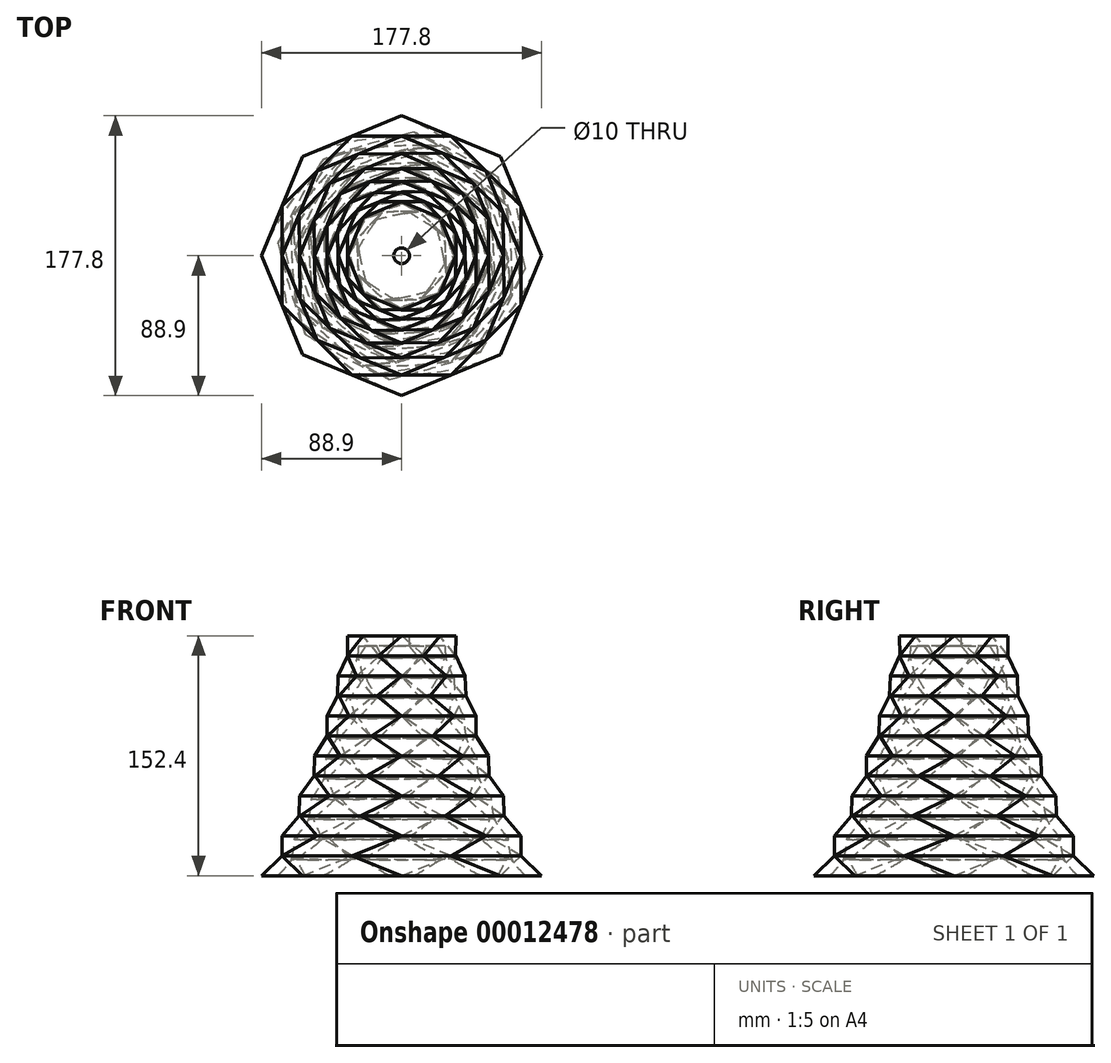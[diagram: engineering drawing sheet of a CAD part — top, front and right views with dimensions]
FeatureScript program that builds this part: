
annotation { "Feature Type Name" : "Feature", "Feature Type Description" : "" }
export const myFeature = defineFeature(function(context is Context, id is Id, definition is map)
    precondition{}
    {
        {
            var Q0;
            Q0=qCreatedBy(makeId("Top.planeOp"),FACE);
            var sketch = newSketch(context, id + "F0", { "sketchPlane" : qUnion([Q0])});
            skLineSegment(sketch, "E0.rect.bottom", {"start": v(88.9, -88.9) * mm, "end": v(-88.9, -88.9) * mm, "construction": true});
            skLineSegment(sketch, "E0.rect.top", {"start": v(88.9, 88.9) * mm, "end": v(-88.9, 88.9) * mm, "construction": true});
            skLineSegment(sketch, "E0.rect.left", {"start": v(88.9, -88.9) * mm, "end": v(88.9, 88.9) * mm, "construction": true});
            skLineSegment(sketch, "E0.rect.right", {"start": v(-88.9, -88.9) * mm, "end": v(-88.9, 88.9) * mm, "construction": true});
            skPoint(sketch, "E0.rect.middle", {"position": v(0, 0) * mm});
            skCircle(sketch, "E1.cCircle", {"center": v(0, 0) * mm, "radius": 88.9 * mm, "construction": true});
            skLineSegment(sketch, "E1.0", {"start": v(88.9, 0) * mm, "end": v(62.86, -62.86) * mm});
            skLineSegment(sketch, "E1.1", {"start": v(62.86, -62.86) * mm, "end": v(0, -88.9) * mm});
            skLineSegment(sketch, "E1.2", {"start": v(0, -88.9) * mm, "end": v(-62.86, -62.86) * mm});
            skLineSegment(sketch, "E1.3", {"start": v(-62.86, -62.86) * mm, "end": v(-88.9, 0) * mm});
            skLineSegment(sketch, "E1.4", {"start": v(-88.9, 0) * mm, "end": v(-62.86, 62.86) * mm});
            skLineSegment(sketch, "E1.5", {"start": v(-62.86, 62.86) * mm, "end": v(0, 88.9) * mm});
            skLineSegment(sketch, "E1.6", {"start": v(0, 88.9) * mm, "end": v(62.86, 62.86) * mm});
            skLineSegment(sketch, "E1.7", {"start": v(62.86, 62.86) * mm, "end": v(88.9, 0) * mm});
            skSolve(sketch);
        }
        {
            var Q0;
            Q0=qCreatedBy(makeId("Top.planeOp"),FACE);
            cPlane(context, id + "F1", {"entities" : qUnion([Q0]), "cplaneType" : CPlaneType.OFFSET, "offset" : 12.7 * mm, "width" : 152.4 * mm, "height" : 152.4 * mm});
        }
        {
            var Q0;
            Q0=qCreatedBy(id+"F1.planeOp",FACE);
            var sketch = newSketch(context, id + "F2", { "sketchPlane" : qUnion([Q0])});
            skPoint(sketch, "E2.0", {"position": v(0, 0) * mm});
            skCircle(sketch, "E3.cCircle", {"center": v(0, 0) * mm, "radius": 82.13 * mm, "construction": true});
            skLineSegment(sketch, "E3.0", {"start": v(75.88, -31.43) * mm, "end": v(31.43, -75.88) * mm});
            skLineSegment(sketch, "E3.1", {"start": v(31.43, -75.88) * mm, "end": v(-31.43, -75.88) * mm});
            skLineSegment(sketch, "E3.2", {"start": v(-31.43, -75.88) * mm, "end": v(-75.88, -31.43) * mm});
            skLineSegment(sketch, "E3.3", {"start": v(-75.88, -31.43) * mm, "end": v(-75.88, 31.43) * mm});
            skLineSegment(sketch, "E3.4", {"start": v(-75.88, 31.43) * mm, "end": v(-31.43, 75.88) * mm});
            skLineSegment(sketch, "E3.5", {"start": v(-31.43, 75.88) * mm, "end": v(31.43, 75.88) * mm});
            skLineSegment(sketch, "E3.6", {"start": v(31.43, 75.88) * mm, "end": v(75.88, 31.43) * mm});
            skLineSegment(sketch, "E3.7", {"start": v(75.88, 31.43) * mm, "end": v(75.88, -31.43) * mm});
            skSolve(sketch);
        }
        {
            var Q0;
            Q0=makeQuery(id+"F0.imprint","IMPRINT",FACE,{"disambiguationData":[TD([[makeQuery(id+"F0.imprint","IMPRINT",EDGE,{"derivedFrom":sQuery(id+"F0.wireOp",EDGE,"E1.0")}),-1.0]])]});
            var Q1;
            Q1=makeQuery(id+"F2.imprint","IMPRINT",FACE,{"disambiguationData":[TD([[makeQuery(id+"F2.imprint","IMPRINT",EDGE,{"derivedFrom":sQuery(id+"F2.wireOp",EDGE,"E3.0")}),-1.0]])]});
            loft(context, id + "F3", {"sheetProfilesArray" : [{ "sheetProfileEntities" : qUnion([Q0]) }, { "sheetProfileEntities" : qUnion([Q1]) }]});
        }
        {
            var Q0;
            Q0=qCreatedBy(id+"F1.planeOp",FACE);
            cPlane(context, id + "F4", {"entities" : qUnion([Q0]), "cplaneType" : CPlaneType.OFFSET, "offset" : 12.7 * mm, "width" : 152.4 * mm, "height" : 152.4 * mm});
        }
        {
            var Q0;
            Q0=qCreatedBy(id+"F4.planeOp",FACE);
            var sketch = newSketch(context, id + "F5", { "sketchPlane" : qUnion([Q0])});
            skFitSpline(sketch, "E4.0", {"points": [v(75.88, -31.43) * mm, v(75.88, -10.48) * mm, v(75.88, 10.48) * mm, v(75.88, 31.43) * mm]});
            skCircle(sketch, "E5.cCircle", {"center": v(0, 0) * mm, "radius": 75.88 * mm, "construction": true});
            skLineSegment(sketch, "E5.0", {"start": v(75.88, 0) * mm, "end": v(53.66, -53.66) * mm});
            skLineSegment(sketch, "E5.1", {"start": v(53.66, -53.66) * mm, "end": v(0, -75.88) * mm});
            skLineSegment(sketch, "E5.2", {"start": v(0, -75.88) * mm, "end": v(-53.66, -53.66) * mm});
            skLineSegment(sketch, "E5.3", {"start": v(-53.66, -53.66) * mm, "end": v(-75.88, 0) * mm});
            skLineSegment(sketch, "E5.4", {"start": v(-75.88, 0) * mm, "end": v(-53.66, 53.66) * mm});
            skLineSegment(sketch, "E5.5", {"start": v(-53.66, 53.66) * mm, "end": v(0, 75.88) * mm});
            skLineSegment(sketch, "E5.6", {"start": v(0, 75.88) * mm, "end": v(53.66, 53.66) * mm});
            skLineSegment(sketch, "E5.7", {"start": v(53.66, 53.66) * mm, "end": v(75.88, 0) * mm});
            skSolve(sketch);
        }
        {
            var Q1;
            Q1=makeQuery(id+"F3.opLoft","CAP_FACE",FACE,{"disambiguationData":[OSD([makeQuery(id+"F2.imprint","IMPRINT",FACE,{"disambiguationData":[TD([[makeQuery(id+"F2.imprint","IMPRINT",EDGE,{"derivedFrom":sQuery(id+"F2.wireOp",EDGE,"E3.0")}),-1.0]])]})])],"isStart":true});
            var Q2;
            Q2=makeQuery(id+"F5.imprint","IMPRINT",FACE,{"disambiguationData":[TD([[makeQuery(id+"F5.imprint","IMPRINT",EDGE,{"derivedFrom":sQuery(id+"F5.wireOp",EDGE,"E5.0")}),-1.0]])]});
            loft(context, id + "F6", {"operationType" : NewBodyOperationType.ADD, "sheetProfilesArray" : [{ "sheetProfileEntities" : qUnion([Q1]) }, { "sheetProfileEntities" : qUnion([Q2]) }]});
        }
        {
            var Q0;
            Q0=qCreatedBy(id+"F4.planeOp",FACE);
            cPlane(context, id + "F7", {"entities" : qUnion([Q0]), "cplaneType" : CPlaneType.OFFSET, "offset" : 12.7 * mm, "width" : 152.4 * mm, "height" : 152.4 * mm});
        }
        {
            var Q0;
            Q0=qCreatedBy(id+"F7.planeOp",FACE);
            var sketch = newSketch(context, id + "F8", { "sketchPlane" : qUnion([Q0])});
            skCircle(sketch, "E6.cCircle", {"center": v(0, 0) * mm, "radius": 70.1 * mm, "construction": true});
            skLineSegment(sketch, "E6.0", {"start": v(64.47, 27.56) * mm, "end": v(65.07, -26.1) * mm});
            skLineSegment(sketch, "E6.1", {"start": v(65.07, -26.1) * mm, "end": v(27.56, -64.47) * mm});
            skLineSegment(sketch, "E6.2", {"start": v(27.56, -64.47) * mm, "end": v(-26.1, -65.07) * mm});
            skLineSegment(sketch, "E6.3", {"start": v(-26.1, -65.07) * mm, "end": v(-64.47, -27.56) * mm});
            skLineSegment(sketch, "E6.4", {"start": v(-64.47, -27.56) * mm, "end": v(-65.07, 26.1) * mm});
            skLineSegment(sketch, "E6.5", {"start": v(-65.07, 26.1) * mm, "end": v(-27.56, 64.47) * mm});
            skLineSegment(sketch, "E6.6", {"start": v(-27.56, 64.47) * mm, "end": v(26.1, 65.07) * mm});
            skLineSegment(sketch, "E6.7", {"start": v(26.1, 65.07) * mm, "end": v(64.47, 27.56) * mm});
            skSolve(sketch);
        }
        {
            var Q1;
            Q1=makeQuery(id+"F6.opLoft","CAP_FACE",FACE,{"disambiguationData":[OSD([makeQuery(id+"F5.imprint","IMPRINT",FACE,{"disambiguationData":[TD([[makeQuery(id+"F5.imprint","IMPRINT",EDGE,{"derivedFrom":sQuery(id+"F5.wireOp",EDGE,"E5.0")}),-1.0]])]})])],"isStart":true});
            var Q2;
            Q2=makeQuery(id+"F8.imprint","IMPRINT",FACE,{"disambiguationData":[TD([[makeQuery(id+"F8.imprint","IMPRINT",EDGE,{"derivedFrom":sQuery(id+"F8.wireOp",EDGE,"E6.0")}),-1.0]])]});
            loft(context, id + "F9", {"operationType" : NewBodyOperationType.ADD, "sheetProfilesArray" : [{ "sheetProfileEntities" : qUnion([Q1]) }, { "sheetProfileEntities" : qUnion([Q2]) }]});
        }
        {
            var Q0;
            Q0=qCreatedBy(id+"F7.planeOp",FACE);
            cPlane(context, id + "F10", {"entities" : qUnion([Q0]), "cplaneType" : CPlaneType.OFFSET, "offset" : 12.7 * mm, "width" : 152.4 * mm, "height" : 152.4 * mm});
        }
        {
            var Q0;
            Q0=qCreatedBy(id+"F10.planeOp",FACE);
            var sketch = newSketch(context, id + "F11", { "sketchPlane" : qUnion([Q0])});
            skCircle(sketch, "E7.cCircle", {"center": v(0, 0) * mm, "radius": 64.78 * mm, "construction": true});
            skLineSegment(sketch, "E7.0", {"start": v(-64.78, 0) * mm, "end": v(-45.8, 45.8) * mm});
            skLineSegment(sketch, "E7.1", {"start": v(-45.8, 45.8) * mm, "end": v(0, 64.78) * mm});
            skLineSegment(sketch, "E7.2", {"start": v(0, 64.78) * mm, "end": v(45.8, 45.8) * mm});
            skLineSegment(sketch, "E7.3", {"start": v(45.8, 45.8) * mm, "end": v(64.78, 0) * mm});
            skLineSegment(sketch, "E7.4", {"start": v(64.78, 0) * mm, "end": v(45.8, -45.8) * mm});
            skLineSegment(sketch, "E7.5", {"start": v(45.8, -45.8) * mm, "end": v(0, -64.78) * mm});
            skLineSegment(sketch, "E7.6", {"start": v(0, -64.78) * mm, "end": v(-45.8, -45.8) * mm});
            skLineSegment(sketch, "E7.7", {"start": v(-45.8, -45.8) * mm, "end": v(-64.78, 0) * mm});
            skSolve(sketch);
        }
        {
            var Q1;
            Q1=makeQuery(id+"F9.opLoft","CAP_FACE",FACE,{"disambiguationData":[OSD([makeQuery(id+"F8.imprint","IMPRINT",FACE,{"disambiguationData":[TD([[makeQuery(id+"F8.imprint","IMPRINT",EDGE,{"derivedFrom":sQuery(id+"F8.wireOp",EDGE,"E6.0")}),-1.0]])]})])],"isStart":true});
            var Q2;
            Q2=makeQuery(id+"F11.imprint","IMPRINT",FACE,{"disambiguationData":[TD([[makeQuery(id+"F11.imprint","IMPRINT",EDGE,{"derivedFrom":sQuery(id+"F11.wireOp",EDGE,"E7.0")}),-1.0]])]});
            loft(context, id + "F12", {"operationType" : NewBodyOperationType.ADD, "sheetProfilesArray" : [{ "sheetProfileEntities" : qUnion([Q1]) }, { "sheetProfileEntities" : qUnion([Q2]) }]});
        }
        {
            var Q0;
            Q0=qCreatedBy(id+"F10.planeOp",FACE);
            cPlane(context, id + "F13", {"entities" : qUnion([Q0]), "cplaneType" : CPlaneType.OFFSET, "offset" : 12.7 * mm, "width" : 152.4 * mm, "height" : 152.4 * mm});
        }
        {
            var Q0;
            Q0=qCreatedBy(id+"F13.planeOp",FACE);
            var sketch = newSketch(context, id + "F14", { "sketchPlane" : qUnion([Q0])});
            skFitSpline(sketch, "E8.0", {"points": [v(64.78, 0) * mm, v(58.45, 15.27) * mm, v(52.13, 30.54) * mm, v(45.8, 45.8) * mm]});
            skCircle(sketch, "E9.cCircle", {"center": v(0, 0) * mm, "radius": 59.85 * mm, "construction": true});
            skLineSegment(sketch, "E9.0", {"start": v(55.07, 23.43) * mm, "end": v(55.51, -22.37) * mm});
            skLineSegment(sketch, "E9.1", {"start": v(55.51, -22.37) * mm, "end": v(23.43, -55.07) * mm});
            skLineSegment(sketch, "E9.2", {"start": v(23.43, -55.07) * mm, "end": v(-22.37, -55.51) * mm});
            skLineSegment(sketch, "E9.3", {"start": v(-22.37, -55.51) * mm, "end": v(-55.07, -23.43) * mm});
            skLineSegment(sketch, "E9.4", {"start": v(-55.07, -23.43) * mm, "end": v(-55.51, 22.37) * mm});
            skLineSegment(sketch, "E9.5", {"start": v(-55.51, 22.37) * mm, "end": v(-23.43, 55.07) * mm});
            skLineSegment(sketch, "E9.6", {"start": v(-23.43, 55.07) * mm, "end": v(22.37, 55.51) * mm});
            skLineSegment(sketch, "E9.7", {"start": v(22.37, 55.51) * mm, "end": v(55.07, 23.43) * mm});
            skSolve(sketch);
        }
        {
            var Q1;
            Q1=makeQuery(id+"F12.opLoft","CAP_FACE",FACE,{"disambiguationData":[OSD([makeQuery(id+"F11.imprint","IMPRINT",FACE,{"disambiguationData":[TD([[makeQuery(id+"F11.imprint","IMPRINT",EDGE,{"derivedFrom":sQuery(id+"F11.wireOp",EDGE,"E7.0")}),-1.0]])]})])],"isStart":true});
            var Q2;
            Q2=makeQuery(id+"F14.imprint","IMPRINT",FACE,{"disambiguationData":[TD([[makeQuery(id+"F14.imprint","IMPRINT",EDGE,{"derivedFrom":sQuery(id+"F14.wireOp",EDGE,"E9.0")}),-1.0]])]});
            loft(context, id + "F15", {"operationType" : NewBodyOperationType.ADD, "sheetProfilesArray" : [{ "sheetProfileEntities" : qUnion([Q1]) }, { "sheetProfileEntities" : qUnion([Q2]) }]});
        }
        {
            var Q0;
            Q0=qCreatedBy(id+"F13.planeOp",FACE);
            cPlane(context, id + "F16", {"entities" : qUnion([Q0]), "cplaneType" : CPlaneType.OFFSET, "offset" : 12.7 * mm, "width" : 152.4 * mm, "height" : 152.4 * mm});
        }
        {
            var Q0;
            Q0=qCreatedBy(id+"F16.planeOp",FACE);
            var sketch = newSketch(context, id + "F17", { "sketchPlane" : qUnion([Q0])});
            skFitSpline(sketch, "E10.0", {"points": [v(55.51, -22.37) * mm, v(55.36, -7.1) * mm, v(55.22, 8.17) * mm, v(55.07, 23.43) * mm]});
            skCircle(sketch, "E11.cCircle", {"center": v(0, 0) * mm, "radius": 55.3 * mm, "construction": true});
            skLineSegment(sketch, "E11.0", {"start": v(55.3, 0) * mm, "end": v(39.1, -39.1) * mm});
            skLineSegment(sketch, "E11.1", {"start": v(39.1, -39.1) * mm, "end": v(0, -55.3) * mm});
            skLineSegment(sketch, "E11.2", {"start": v(0, -55.3) * mm, "end": v(-39.1, -39.1) * mm});
            skLineSegment(sketch, "E11.3", {"start": v(-39.1, -39.1) * mm, "end": v(-55.3, 0) * mm});
            skLineSegment(sketch, "E11.4", {"start": v(-55.3, 0) * mm, "end": v(-39.1, 39.1) * mm});
            skLineSegment(sketch, "E11.5", {"start": v(-39.1, 39.1) * mm, "end": v(0, 55.3) * mm});
            skLineSegment(sketch, "E11.6", {"start": v(0, 55.3) * mm, "end": v(39.1, 39.1) * mm});
            skLineSegment(sketch, "E11.7", {"start": v(39.1, 39.1) * mm, "end": v(55.3, 0) * mm});
            skSolve(sketch);
        }
        {
            var Q1;
            Q1=makeQuery(id+"F15.opLoft","CAP_FACE",FACE,{"disambiguationData":[OSD([makeQuery(id+"F14.imprint","IMPRINT",FACE,{"disambiguationData":[TD([[makeQuery(id+"F14.imprint","IMPRINT",EDGE,{"derivedFrom":sQuery(id+"F14.wireOp",EDGE,"E9.0")}),-1.0]])]})])],"isStart":true});
            var Q2;
            Q2=makeQuery(id+"F17.imprint","IMPRINT",FACE,{"disambiguationData":[TD([[makeQuery(id+"F17.imprint","IMPRINT",EDGE,{"derivedFrom":sQuery(id+"F17.wireOp",EDGE,"E11.0")}),-1.0]])]});
            loft(context, id + "F18", {"operationType" : NewBodyOperationType.ADD, "sheetProfilesArray" : [{ "sheetProfileEntities" : qUnion([Q1]) }, { "sheetProfileEntities" : qUnion([Q2]) }]});
        }
        {
            var Q0;
            Q0=qCreatedBy(id+"F16.planeOp",FACE);
            cPlane(context, id + "F19", {"entities" : qUnion([Q0]), "cplaneType" : CPlaneType.OFFSET, "offset" : 12.7 * mm, "width" : 152.4 * mm, "height" : 152.4 * mm});
        }
        {
            var Q0;
            Q0=qCreatedBy(id+"F19.planeOp",FACE);
            var sketch = newSketch(context, id + "F20", { "sketchPlane" : qUnion([Q0])});
            skCircle(sketch, "E12.cCircle", {"center": v(0, 0) * mm, "radius": 51.09 * mm, "construction": true});
            skLineSegment(sketch, "E12.0", {"start": v(46.97, 20.1) * mm, "end": v(47.43, -19) * mm});
            skLineSegment(sketch, "E12.1", {"start": v(47.43, -19) * mm, "end": v(20.1, -46.97) * mm});
            skLineSegment(sketch, "E12.2", {"start": v(20.1, -46.97) * mm, "end": v(-19, -47.43) * mm});
            skLineSegment(sketch, "E12.3", {"start": v(-19, -47.43) * mm, "end": v(-46.97, -20.1) * mm});
            skLineSegment(sketch, "E12.4", {"start": v(-46.97, -20.1) * mm, "end": v(-47.43, 19) * mm});
            skLineSegment(sketch, "E12.5", {"start": v(-47.43, 19) * mm, "end": v(-20.1, 46.97) * mm});
            skLineSegment(sketch, "E12.6", {"start": v(-20.1, 46.97) * mm, "end": v(19, 47.43) * mm});
            skLineSegment(sketch, "E12.7", {"start": v(19, 47.43) * mm, "end": v(46.97, 20.1) * mm});
            skSolve(sketch);
        }
        {
            var Q1;
            Q1=makeQuery(id+"F18.opLoft","CAP_FACE",FACE,{"disambiguationData":[OSD([makeQuery(id+"F17.imprint","IMPRINT",FACE,{"disambiguationData":[TD([[makeQuery(id+"F17.imprint","IMPRINT",EDGE,{"derivedFrom":sQuery(id+"F17.wireOp",EDGE,"E11.0")}),-1.0]])]})])],"isStart":true});
            var Q2;
            Q2=makeQuery(id+"F20.imprint","IMPRINT",FACE,{"disambiguationData":[TD([[makeQuery(id+"F20.imprint","IMPRINT",EDGE,{"derivedFrom":sQuery(id+"F20.wireOp",EDGE,"E12.0")}),-1.0]])]});
            loft(context, id + "F21", {"operationType" : NewBodyOperationType.ADD, "sheetProfilesArray" : [{ "sheetProfileEntities" : qUnion([Q1]) }, { "sheetProfileEntities" : qUnion([Q2]) }]});
        }
        {
            var Q0;
            Q0=qCreatedBy(id+"F19.planeOp",FACE);
            cPlane(context, id + "F22", {"entities" : qUnion([Q0]), "cplaneType" : CPlaneType.OFFSET, "offset" : 12.7 * mm, "width" : 152.4 * mm, "height" : 152.4 * mm});
        }
        {
            var Q0;
            Q0=qCreatedBy(id+"F22.planeOp",FACE);
            var sketch = newSketch(context, id + "F23", { "sketchPlane" : qUnion([Q0])});
            skCircle(sketch, "E13.cCircle", {"center": v(0, 0) * mm, "radius": 47.2 * mm, "construction": true});
            skLineSegment(sketch, "E13.0", {"start": v(47.2, 0) * mm, "end": v(33.38, -33.38) * mm});
            skLineSegment(sketch, "E13.1", {"start": v(33.38, -33.38) * mm, "end": v(0, -47.2) * mm});
            skLineSegment(sketch, "E13.2", {"start": v(0, -47.2) * mm, "end": v(-33.38, -33.38) * mm});
            skLineSegment(sketch, "E13.3", {"start": v(-33.38, -33.38) * mm, "end": v(-47.2, 0) * mm});
            skLineSegment(sketch, "E13.4", {"start": v(-47.2, 0) * mm, "end": v(-33.38, 33.38) * mm});
            skLineSegment(sketch, "E13.5", {"start": v(-33.38, 33.38) * mm, "end": v(0, 47.2) * mm});
            skLineSegment(sketch, "E13.6", {"start": v(0, 47.2) * mm, "end": v(33.38, 33.38) * mm});
            skLineSegment(sketch, "E13.7", {"start": v(33.38, 33.38) * mm, "end": v(47.2, 0) * mm});
            skSolve(sketch);
        }
        {
            var Q1;
            Q1=makeQuery(id+"F21.opLoft","CAP_FACE",FACE,{"disambiguationData":[OSD([makeQuery(id+"F20.imprint","IMPRINT",FACE,{"disambiguationData":[TD([[makeQuery(id+"F20.imprint","IMPRINT",EDGE,{"derivedFrom":sQuery(id+"F20.wireOp",EDGE,"E12.0")}),-1.0]])]})])],"isStart":true});
            var Q2;
            Q2=makeQuery(id+"F23.imprint","IMPRINT",FACE,{"disambiguationData":[TD([[makeQuery(id+"F23.imprint","IMPRINT",EDGE,{"derivedFrom":sQuery(id+"F23.wireOp",EDGE,"E13.0")}),-1.0]])]});
            loft(context, id + "F24", {"operationType" : NewBodyOperationType.ADD, "sheetProfilesArray" : [{ "sheetProfileEntities" : qUnion([Q1]) }, { "sheetProfileEntities" : qUnion([Q2]) }]});
        }
        {
            var Q0;
            Q0=qCreatedBy(id+"F22.planeOp",FACE);
            cPlane(context, id + "F25", {"entities" : qUnion([Q0]), "cplaneType" : CPlaneType.OFFSET, "offset" : 12.7 * mm, "width" : 152.4 * mm, "height" : 152.4 * mm});
        }
        {
            var Q0;
            Q0=qCreatedBy(id+"F25.planeOp",FACE);
            var sketch = newSketch(context, id + "F26", { "sketchPlane" : qUnion([Q0])});
            skCircle(sketch, "E14.cCircle", {"center": v(0, 0) * mm, "radius": 43.63 * mm, "construction": true});
            skLineSegment(sketch, "E14.0", {"start": v(39.79, 17.9) * mm, "end": v(40.8, -15.47) * mm});
            skLineSegment(sketch, "E14.1", {"start": v(40.8, -15.47) * mm, "end": v(17.9, -39.79) * mm});
            skLineSegment(sketch, "E14.2", {"start": v(17.9, -39.79) * mm, "end": v(-15.47, -40.8) * mm});
            skLineSegment(sketch, "E14.3", {"start": v(-15.47, -40.8) * mm, "end": v(-39.79, -17.9) * mm});
            skLineSegment(sketch, "E14.4", {"start": v(-39.79, -17.9) * mm, "end": v(-40.8, 15.47) * mm});
            skLineSegment(sketch, "E14.5", {"start": v(-40.8, 15.47) * mm, "end": v(-17.9, 39.79) * mm});
            skLineSegment(sketch, "E14.6", {"start": v(-17.9, 39.79) * mm, "end": v(15.47, 40.8) * mm});
            skLineSegment(sketch, "E14.7", {"start": v(15.47, 40.8) * mm, "end": v(39.79, 17.9) * mm});
            skSolve(sketch);
        }
        {
            var Q1;
            Q1=makeQuery(id+"F24.opLoft","CAP_FACE",FACE,{"disambiguationData":[OSD([makeQuery(id+"F23.imprint","IMPRINT",FACE,{"disambiguationData":[TD([[makeQuery(id+"F23.imprint","IMPRINT",EDGE,{"derivedFrom":sQuery(id+"F23.wireOp",EDGE,"E13.0")}),-1.0]])]})])],"isStart":true});
            var Q2;
            Q2=makeQuery(id+"F26.imprint","IMPRINT",FACE,{"disambiguationData":[TD([[makeQuery(id+"F26.imprint","IMPRINT",EDGE,{"derivedFrom":sQuery(id+"F26.wireOp",EDGE,"E14.0")}),-1.0]])]});
            loft(context, id + "F27", {"operationType" : NewBodyOperationType.ADD, "sheetProfilesArray" : [{ "sheetProfileEntities" : qUnion([Q1]) }, { "sheetProfileEntities" : qUnion([Q2]) }]});
        }
        {
            var Q0;
            Q0=qCreatedBy(id+"F25.planeOp",FACE);
            cPlane(context, id + "F28", {"entities" : qUnion([Q0]), "cplaneType" : CPlaneType.OFFSET, "offset" : 12.7 * mm, "width" : 152.4 * mm, "height" : 152.4 * mm});
        }
        {
            var Q0;
            Q0=qCreatedBy(id+"F28.planeOp",FACE);
            var sketch = newSketch(context, id + "F29", { "sketchPlane" : qUnion([Q0])});
            skCircle(sketch, "E15.cCircle", {"center": v(0, 0) * mm, "radius": 40.33 * mm, "construction": true});
            skLineSegment(sketch, "E15.0", {"start": v(40.33, 0) * mm, "end": v(28.52, -28.52) * mm});
            skLineSegment(sketch, "E15.1", {"start": v(28.52, -28.52) * mm, "end": v(0, -40.33) * mm});
            skLineSegment(sketch, "E15.2", {"start": v(0, -40.33) * mm, "end": v(-28.52, -28.52) * mm});
            skLineSegment(sketch, "E15.3", {"start": v(-28.52, -28.52) * mm, "end": v(-40.33, 0) * mm});
            skLineSegment(sketch, "E15.4", {"start": v(-40.33, 0) * mm, "end": v(-28.52, 28.52) * mm});
            skLineSegment(sketch, "E15.5", {"start": v(-28.52, 28.52) * mm, "end": v(0, 40.33) * mm});
            skLineSegment(sketch, "E15.6", {"start": v(0, 40.33) * mm, "end": v(28.52, 28.52) * mm});
            skLineSegment(sketch, "E15.7", {"start": v(28.52, 28.52) * mm, "end": v(40.33, 0) * mm});
            skSolve(sketch);
        }
        {
            var Q1;
            Q1=makeQuery(id+"F27.opLoft","CAP_FACE",FACE,{"disambiguationData":[OSD([makeQuery(id+"F26.imprint","IMPRINT",FACE,{"disambiguationData":[TD([[makeQuery(id+"F26.imprint","IMPRINT",EDGE,{"derivedFrom":sQuery(id+"F26.wireOp",EDGE,"E14.0")}),-1.0]])]})])],"isStart":true});
            var Q2;
            Q2=makeQuery(id+"F29.imprint","IMPRINT",FACE,{"disambiguationData":[TD([[makeQuery(id+"F29.imprint","IMPRINT",EDGE,{"derivedFrom":sQuery(id+"F29.wireOp",EDGE,"E15.0")}),-1.0]])]});
            loft(context, id + "F30", {"operationType" : NewBodyOperationType.ADD, "sheetProfilesArray" : [{ "sheetProfileEntities" : qUnion([Q1]) }, { "sheetProfileEntities" : qUnion([Q2]) }]});
        }
        {
            var Q0;
            Q0=qCreatedBy(id+"F28.planeOp",FACE);
            cPlane(context, id + "F31", {"entities" : qUnion([Q0]), "cplaneType" : CPlaneType.OFFSET, "offset" : 12.7 * mm, "width" : 152.4 * mm, "height" : 152.4 * mm});
        }
        {
            var Q0;
            Q0=qCreatedBy(id+"F31.planeOp",FACE);
            var sketch = newSketch(context, id + "F32", { "sketchPlane" : qUnion([Q0])});
            skFitSpline(sketch, "E16.0", {"points": [v(-40.33, 0) * mm, v(-36.4, -9.5) * mm, v(-32.45, -19.01) * mm, v(-28.52, -28.52) * mm]});
            skCircle(sketch, "E17.cCircle", {"center": v(0, 0) * mm, "radius": 37.26 * mm, "construction": true});
            skLineSegment(sketch, "E17.0", {"start": v(-34.53, -14) * mm, "end": v(-34.31, 14.53) * mm});
            skLineSegment(sketch, "E17.1", {"start": v(-34.31, 14.53) * mm, "end": v(-14, 34.53) * mm});
            skLineSegment(sketch, "E17.2", {"start": v(-14, 34.53) * mm, "end": v(14.53, 34.31) * mm});
            skLineSegment(sketch, "E17.3", {"start": v(14.53, 34.31) * mm, "end": v(34.53, 14) * mm});
            skLineSegment(sketch, "E17.4", {"start": v(34.53, 14) * mm, "end": v(34.31, -14.53) * mm});
            skLineSegment(sketch, "E17.5", {"start": v(34.31, -14.53) * mm, "end": v(14, -34.53) * mm});
            skLineSegment(sketch, "E17.6", {"start": v(14, -34.53) * mm, "end": v(-14.53, -34.31) * mm});
            skLineSegment(sketch, "E17.7", {"start": v(-14.53, -34.31) * mm, "end": v(-34.53, -14) * mm});
            skSolve(sketch);
        }
        {
            var Q1;
            Q1=makeQuery(id+"F30.opLoft","CAP_FACE",FACE,{"disambiguationData":[OSD([makeQuery(id+"F29.imprint","IMPRINT",FACE,{"disambiguationData":[TD([[makeQuery(id+"F29.imprint","IMPRINT",EDGE,{"derivedFrom":sQuery(id+"F29.wireOp",EDGE,"E15.0")}),-1.0]])]})])],"isStart":true});
            var Q2;
            Q2=makeQuery(id+"F32.imprint","IMPRINT",FACE,{"disambiguationData":[TD([[makeQuery(id+"F32.imprint","IMPRINT",EDGE,{"derivedFrom":sQuery(id+"F32.wireOp",EDGE,"E17.0")}),-1.0]])]});
            var Q3;
            Q3=makeQuery(id+"F30.opLoft","MID_CAP_VERTEX",VERTEX,{"disambiguationData":[OSD([sQuery(id+"F29.wireOp",EDGE,"E15.0"),sQuery(id+"F29.wireOp",EDGE,"E15.1")])],"capPos":1.0});
            var Q4;
            Q4=sQuery(id+"F32.wireOp",VERTEX,"E17.6.start");
            loft(context, id + "F33", {"operationType" : NewBodyOperationType.ADD, "sheetProfilesArray" : [{ "sheetProfileEntities" : qUnion([Q1]) }, { "sheetProfileEntities" : qUnion([Q2]) }], "matchConnections" : true, "connections" : [{ "connectionEntities" : qUnion([Q3, Q4]), "connectionEdgeQueries" : qUnion([]), "connectionEdgeParameters" : [] }]});
        }
        {
            var Q0;
            Q0=qCreatedBy(id+"F31.planeOp",FACE);
            cPlane(context, id + "F34", {"entities" : qUnion([Q0]), "cplaneType" : CPlaneType.OFFSET, "offset" : 12.7 * mm, "width" : 152.4 * mm, "height" : 152.4 * mm});
        }
        {
            var Q0;
            Q0=qCreatedBy(id+"F34.planeOp",FACE);
            var sketch = newSketch(context, id + "F35", { "sketchPlane" : qUnion([Q0])});
            skCircle(sketch, "E18.cCircle", {"center": v(0, 0) * mm, "radius": 34.42 * mm, "construction": true});
            skLineSegment(sketch, "E18.0", {"start": v(-34.42, 0) * mm, "end": v(-24.34, 24.34) * mm});
            skLineSegment(sketch, "E18.1", {"start": v(-24.34, 24.34) * mm, "end": v(0, 34.42) * mm});
            skLineSegment(sketch, "E18.2", {"start": v(0, 34.42) * mm, "end": v(24.34, 24.34) * mm});
            skLineSegment(sketch, "E18.3", {"start": v(24.34, 24.34) * mm, "end": v(34.42, 0) * mm});
            skLineSegment(sketch, "E18.4", {"start": v(34.42, 0) * mm, "end": v(24.34, -24.34) * mm});
            skLineSegment(sketch, "E18.5", {"start": v(24.34, -24.34) * mm, "end": v(0, -34.42) * mm});
            skLineSegment(sketch, "E18.6", {"start": v(0, -34.42) * mm, "end": v(-24.34, -24.34) * mm});
            skLineSegment(sketch, "E18.7", {"start": v(-24.34, -24.34) * mm, "end": v(-34.42, 0) * mm});
            skSolve(sketch);
        }
        {
            var Q1;
            Q1=makeQuery(id+"F33.opLoft","CAP_FACE",FACE,{"disambiguationData":[OSD([makeQuery(id+"F32.imprint","IMPRINT",FACE,{"disambiguationData":[TD([[makeQuery(id+"F32.imprint","IMPRINT",EDGE,{"derivedFrom":sQuery(id+"F32.wireOp",EDGE,"E17.0")}),-1.0]])]})])],"isStart":true});
            var Q2;
            Q2=makeQuery(id+"F35.imprint","IMPRINT",FACE,{"disambiguationData":[TD([[makeQuery(id+"F35.imprint","IMPRINT",EDGE,{"derivedFrom":sQuery(id+"F35.wireOp",EDGE,"E18.0")}),-1.0]])]});
            var Q3;
            Q3=makeQuery(id+"F33.opLoft","MID_CAP_VERTEX",VERTEX,{"disambiguationData":[OSD([sQuery(id+"F32.wireOp",EDGE,"E17.6"),sQuery(id+"F32.wireOp",EDGE,"E17.7")])],"capPos":1.0});
            var Q4;
            Q4=sQuery(id+"F35.wireOp",VERTEX,"E18.6.start");
            loft(context, id + "F36", {"operationType" : NewBodyOperationType.ADD, "sheetProfilesArray" : [{ "sheetProfileEntities" : qUnion([Q1]) }, { "sheetProfileEntities" : qUnion([Q2]) }], "matchConnections" : true, "connections" : [{ "connectionEntities" : qUnion([Q3, Q4]), "connectionEdgeQueries" : qUnion([]), "connectionEdgeParameters" : [] }]});
        }
        {
            var Q0;
            Q0=makeQuery(id+"F3.opLoft","CAP_FACE",FACE,{"disambiguationData":[OSD([makeQuery(id+"F0.imprint","IMPRINT",FACE,{"disambiguationData":[TD([[makeQuery(id+"F0.imprint","IMPRINT",EDGE,{"derivedFrom":sQuery(id+"F0.wireOp",EDGE,"E1.0")}),-1.0]])]})])],"isStart":true});
            shell(context, id + "F37", {"entities" : qUnion([Q0]), "thickness" : 6.35 * mm});
        }
        {
            var Q0;
            Q0=qCreatedBy(id+"F34.planeOp",FACE);
            var sketch = newSketch(context, id + "F38", { "sketchPlane" : qUnion([Q0])});
            skCircle(sketch, "E19", {"center": v(0, 0) * mm, "radius": 5 * mm});
            skSolve(sketch);
        }
        {
            var Q0;
            Q0 = qSketchRegion(id + "F38", true);
            extrude(context, id + "F39", {"entities" : qUnion([Q0]), "operationType" : NewBodyOperationType.REMOVE, "oppositeDirection" : true, "depth" : 25 * mm});
        }
    });
